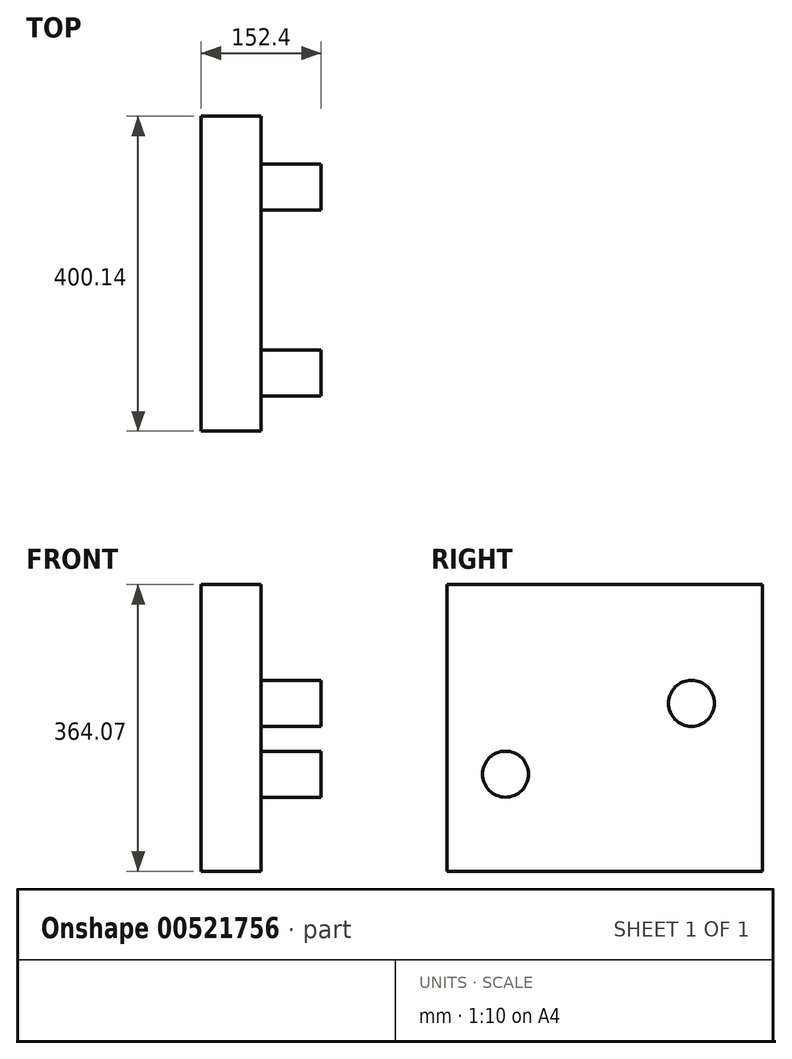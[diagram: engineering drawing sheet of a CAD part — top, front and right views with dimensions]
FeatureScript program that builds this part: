
annotation { "Feature Type Name" : "Feature", "Feature Type Description" : "" }
export const myFeature = defineFeature(function(context is Context, id is Id, definition is map)
    precondition{}
    {
        {
            var Q0;
            Q0=qCreatedBy(makeId("Right.planeOp"),FACE);
            var sketch = newSketch(context, id + "F0", { "sketchPlane" : qUnion([Q0])});
            skLineSegment(sketch, "E0.bottom", {"start": v(-209.05, 240.7) * mm, "end": v(191.1, 240.7) * mm});
            skLineSegment(sketch, "E0.top", {"start": v(-209.05, -123.37) * mm, "end": v(191.1, -123.37) * mm});
            skLineSegment(sketch, "E0.left", {"start": v(-209.05, 240.7) * mm, "end": v(-209.05, -123.37) * mm});
            skLineSegment(sketch, "E0.right", {"start": v(191.1, 240.7) * mm, "end": v(191.1, -123.37) * mm});
            skSolve(sketch);
        }
        {
            var Q0;
            Q0=makeQuery(id+"F0.imprint","IMPRINT",FACE,{"disambiguationData":[TD([[makeQuery(id+"F0.imprint","IMPRINT",EDGE,{"derivedFrom":sQuery(id+"F0.wireOp",EDGE,"E0.bottom")}),-1.0]])]});
            var sketch = newSketch(context, id + "F1", { "sketchPlane" : qUnion([Q0])});
            skCircle(sketch, "E1", {"center": v(-134.98, 0) * mm, "radius": 29.21 * mm});
            skCircle(sketch, "E2", {"center": v(101.24, 90) * mm, "radius": 29.21 * mm});
            skSolve(sketch);
        }
        {
            var Q0;
            Q0=makeQuery(id+"F0.imprint","IMPRINT",FACE,{"disambiguationData":[TD([[makeQuery(id+"F0.imprint","IMPRINT",EDGE,{"derivedFrom":sQuery(id+"F0.wireOp",EDGE,"E0.bottom")}),-1.0]])]});
            extrude(context, id + "F2", {"entities" : qUnion([Q0]), "oppositeDirection" : true, "depth" : 76.2 * mm, "offsetDistance" : 25.4 * mm});
        }
        {
            var Q0;
            Q0=makeQuery(id+"F1.imprint","IMPRINT",FACE,{"disambiguationData":[TD([[makeQuery(id+"F1.imprint","IMPRINT",EDGE,{"derivedFrom":sQuery(id+"F1.wireOp",EDGE,"E1")}),1.0]])]});
            var Q1;
            Q1=makeQuery(id+"F1.imprint","IMPRINT",FACE,{"disambiguationData":[TD([[makeQuery(id+"F1.imprint","IMPRINT",EDGE,{"derivedFrom":sQuery(id+"F1.wireOp",EDGE,"E2")}),1.0]])]});
            extrude(context, id + "F3", {"entities" : qUnion([Q0, Q1]), "operationType" : NewBodyOperationType.ADD, "depth" : 76.2 * mm, "offsetDistance" : 25.4 * mm});
        }
    });
